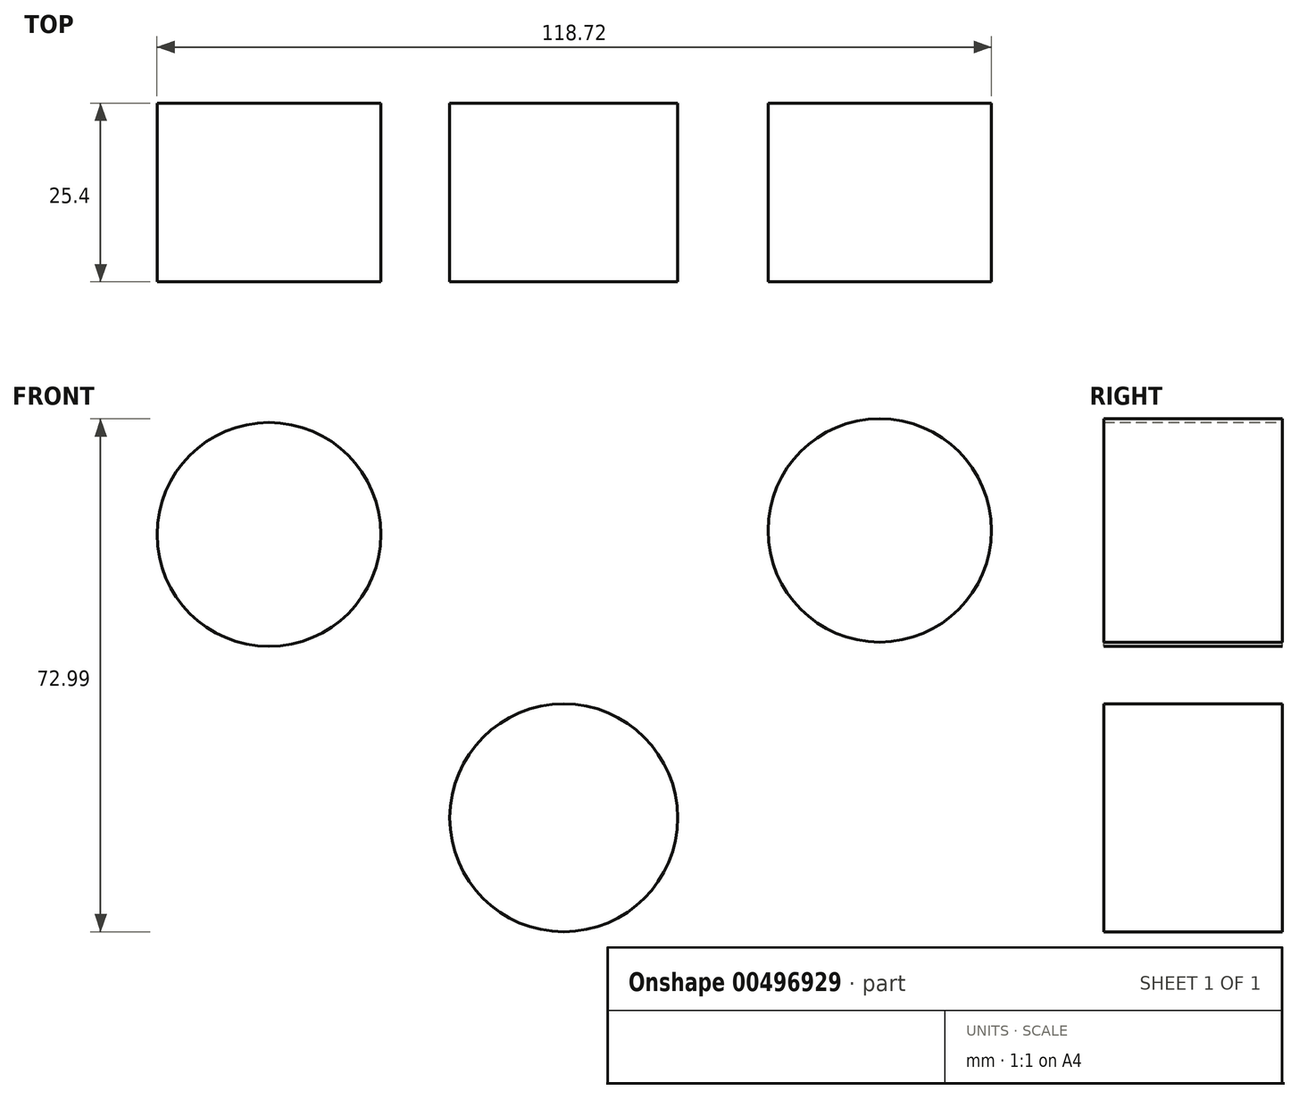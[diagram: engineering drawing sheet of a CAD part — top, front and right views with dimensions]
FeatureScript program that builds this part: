
annotation { "Feature Type Name" : "Feature", "Feature Type Description" : "" }
export const myFeature = defineFeature(function(context is Context, id is Id, definition is map)
    precondition{}
    {
        {
            var Q0;
            Q0=qCreatedBy(makeId("Front.planeOp"),FACE);
            var sketch = newSketch(context, id + "F0", { "sketchPlane" : qUnion([Q0])});
            skCircle(sketch, "E0", {"center": v(0, 0) * mm, "radius": 16.21 * mm});
            skSolve(sketch);
        }
        {
            var Q0;
            Q0 = qSketchRegion(id + "F0", true);
            extrude(context, id + "F1", {"entities" : qUnion([Q0]), "depth" : 25.4 * mm});
        }
        {
            var Q0;
            Q0=qCreatedBy(makeId("Front.planeOp"),FACE);
            var sketch = newSketch(context, id + "F2", { "sketchPlane" : qUnion([Q0])});
            skCircle(sketch, "E1", {"center": v(-41.94, 40.33) * mm, "radius": 15.93 * mm});
            skCircle(sketch, "E2", {"center": v(0, 0) * mm, "radius": 16.12 * mm});
            skSolve(sketch);
        }
        {
            var Q0;
            Q0 = qSketchRegion(id + "F2", true);
            extrude(context, id + "F3", {"entities" : qUnion([Q0]), "operationType" : NewBodyOperationType.ADD, "depth" : 25.4 * mm});
        }
        {
            var Q0;
            Q0=qCreatedBy(makeId("Front.planeOp"),FACE);
            var sketch = newSketch(context, id + "F4", { "sketchPlane" : qUnion([Q0])});
            skCircle(sketch, "E3", {"center": v(44.96, 40.9) * mm, "radius": 15.9 * mm});
            skSolve(sketch);
        }
        {
            var Q0;
            Q0=makeQuery(id+"F4.imprint","IMPRINT",FACE,{"disambiguationData":[TD([[makeQuery(id+"F4.imprint","IMPRINT",EDGE,{"derivedFrom":sQuery(id+"F4.wireOp",EDGE,"E3")}),1.0]])]});
            extrude(context, id + "F5", {"entities" : qUnion([Q0]), "depth" : 25.4 * mm});
        }
    });
